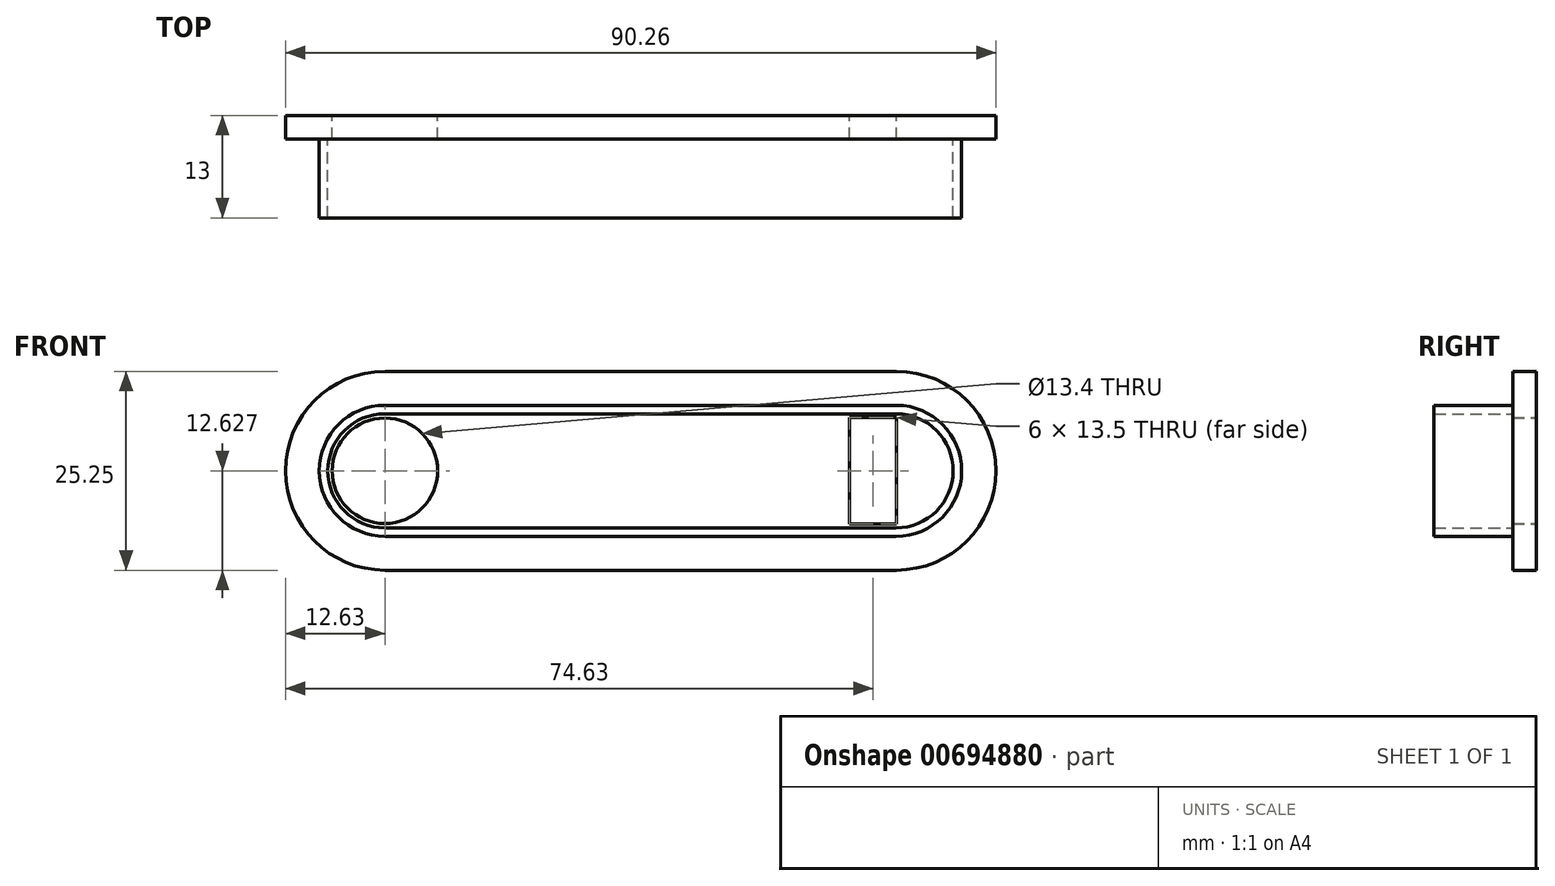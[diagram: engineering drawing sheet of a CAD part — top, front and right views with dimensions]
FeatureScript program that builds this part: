
annotation { "Feature Type Name" : "Feature", "Feature Type Description" : "" }
export const myFeature = defineFeature(function(context is Context, id is Id, definition is map)
    precondition{}
    {
        {
            var Q0;
            Q0=qCreatedBy(makeId("Front.planeOp"),FACE);
            var sketch = newSketch(context, id + "F0", { "sketchPlane" : qUnion([Q0])});
            skLineSegment(sketch, "E0.bottom", {"start": v(19.83, -12.27) * mm, "end": v(-45.17, -12.27) * mm});
            skLineSegment(sketch, "E0.top", {"start": v(19.83, 12.98) * mm, "end": v(-45.17, 12.98) * mm});
            skArc(sketch, "E1", {"start": v(-45.17, 12.98) * mm, "mid": v(-57.8, 0.36) * mm, "end": v(-45.17, -12.27) * mm});
            skArc(sketch, "E2", {"start": v(19.83, -12.27) * mm, "mid": v(32.46, 0.36) * mm, "end": v(19.83, 12.98) * mm});
            skCircle(sketch, "E3", {"center": v(-45.17, 0.36) * mm, "radius": 6.7 * mm});
            skLineSegment(sketch, "E4", {"start": v(19.83, 7.6) * mm, "end": v(12.83, 7.6) * mm});
            skLineSegment(sketch, "E5", {"start": v(12.83, 7.6) * mm, "end": v(19.83, 7.6) * mm});
            skLineSegment(sketch, "E6", {"start": v(19.77, -6.9) * mm, "end": v(12.83, -6.9) * mm});
            skLineSegment(sketch, "E7", {"start": v(19.83, -9.14) * mm, "end": v(19.83, -9.64) * mm});
            skLineSegment(sketch, "E8", {"start": v(13.77, -6.9) * mm, "end": v(19.77, -6.9) * mm});
            skLineSegment(sketch, "E9", {"start": v(19.83, 12.98) * mm, "end": v(19.83, 8.68) * mm});
            skLineSegment(sketch, "E10", {"start": v(19.83, 8.68) * mm, "end": v(-45.17, 8.68) * mm});
            skLineSegment(sketch, "E11", {"start": v(-45.17, -12.27) * mm, "end": v(-45.17, -7.97) * mm});
            skLineSegment(sketch, "E12", {"start": v(-45.17, -7.97) * mm, "end": v(19.77, -7.97) * mm});
            skLineSegment(sketch, "E13", {"start": v(19.77, -6.9) * mm, "end": v(-45.17, -6.9) * mm});
            skLineSegment(sketch, "E14", {"start": v(19.83, 7.6) * mm, "end": v(-45.17, 7.6) * mm});
            skArc(sketch, "E15", {"start": v(-45.17, 8.68) * mm, "mid": v(-53.5, 0.36) * mm, "end": v(-45.17, -7.97) * mm});
            skArc(sketch, "E16", {"start": v(-45.17, 7.6) * mm, "mid": v(-52.42, 0.36) * mm, "end": v(-45.17, -6.9) * mm});
            skLineSegment(sketch, "E17", {"start": v(19.83, 12.98) * mm, "end": v(19.83, -12.27) * mm});
            skPoint(sketch, "E18.middle", {"position": v(16.83, 0.36) * mm});
            skLineSegment(sketch, "E19", {"start": v(19.83, 0.36) * mm, "end": v(19.83, 7.1) * mm});
            skLineSegment(sketch, "E20", {"start": v(19.83, 7.1) * mm, "end": v(13.83, 7.1) * mm});
            skLineSegment(sketch, "E21", {"start": v(13.83, 7.1) * mm, "end": v(13.83, -6.4) * mm});
            skLineSegment(sketch, "E22", {"start": v(13.83, -6.4) * mm, "end": v(19.83, -6.4) * mm});
            skLineSegment(sketch, "E23", {"start": v(19.83, -6.4) * mm, "end": v(19.83, 7.1) * mm});
            skArc(sketch, "E24", {"start": v(19.77, -7.97) * mm, "mid": v(28.1, 0.33) * mm, "end": v(19.83, 8.68) * mm});
            skArc(sketch, "E25", {"start": v(19.77, -6.9) * mm, "mid": v(27.02, 0.33) * mm, "end": v(19.83, 7.6) * mm});
            skSolve(sketch);
        }
        {
            var Q0;
            {var subQ7=sQuery(id+"F0.wireOp",EDGE,"51b1c564-5096-461f-b846-86fedcb4dc8d");Q0=makeQuery(id+"F0.imprint","IMPRINT",FACE,{"disambiguationData":[TD([[makeQuery(id+"F0.imprint","IMPRINT",EDGE,{"derivedFrom":subQ7}),-1.0]])]});}
            var Q1;
            {var subQ2=sQuery(id+"F0.wireOp",EDGE,"E10");Q1=makeQuery(id+"F0.imprint","IMPRINT",FACE,{"disambiguationData":[TD([[makeQuery(id+"F0.imprint","IMPRINT",EDGE,{"derivedFrom":subQ2}),1.0]])]});}
            var Q2;
            {var subQ1=sQuery(id+"F0.wireOp",EDGE,"E17");var subQ3=sQuery(id+"F0.wireOp",EDGE,"E25");var subQ5=makeQuery(id+"F0.imprint","INTERSECT",VERTEX,{"derivedFrom":[subQ1,subQ3]});Q2=makeQuery(id+"F0.imprint","IMPRINT",FACE,{"disambiguationData":[TD([[makeQuery(id+"F0.imprint","IMPRINT",EDGE,{"disambiguationData":[TD([[subQ5,-1.0]])],"derivedFrom":subQ1}),1.0]])]});}
            var Q3;
            Q3=sQuery(id+"F0.wireOp",EDGE,"E0.bottom");
            var Q4;
            Q4=sQuery(id+"F0.wireOp",EDGE,"E0.top");
            var Q5;
            Q5=sQuery(id+"F0.wireOp",EDGE,"E1");
            var Q6;
            Q6=sQuery(id+"F0.wireOp",EDGE,"E2");
            var Q7;
            Q7=sQuery(id+"F0.wireOp",EDGE,"b6ad355e-3722-486a-9c23-38b4642f48d5");
            var Q8;
            Q8=sQuery(id+"F0.wireOp",EDGE,"a5da55c1-d781-4ce2-bdd2-e8d78816f261");
            var Q9;
            Q9=sQuery(id+"F0.wireOp",EDGE,"4fcaac24-b5ef-42e9-b2ac-9cf3cb188516");
            var Q10;
            Q10=sQuery(id+"F0.wireOp",EDGE,"628284f1-229c-46e7-b658-0923db650eb1");
            var Q11;
            Q11=sQuery(id+"F0.wireOp",EDGE,"ba1896cc-4fff-441c-831c-8a4a6f83a2d8");
            var Q12;
            Q12=sQuery(id+"F0.wireOp",EDGE,"E3");
            var Q13;
            Q13=sQuery(id+"F0.wireOp",EDGE,"51b1c564-5096-461f-b846-86fedcb4dc8d");
            var Q14;
            Q14=sQuery(id+"F0.wireOp",EDGE,"6838ca93-eeed-4bdc-afd8-a1c92112be62");
            var Q15;
            Q15=sQuery(id+"F0.wireOp",EDGE,"796d279d-d692-426c-9acc-43a315af8945");
            var Q16;
            Q16=sQuery(id+"F0.wireOp",EDGE,"468f62cb-83c4-4c1b-bd70-739f3564f4d7");
            var Q17;
            Q17=sQuery(id+"F0.wireOp",EDGE,"63cf6457-4c57-4bea-b750-75ee11e2a53f");
            var Q18;
            Q18=sQuery(id+"F0.wireOp",EDGE,"e143a53b-bbf0-4694-9fd8-2c268869048d");
            var Q19;
            Q19=sQuery(id+"F0.wireOp",EDGE,"8f19fd11-0280-4987-803d-bc3ecc1a1e02");
            var Q20;
            Q20=sQuery(id+"F0.wireOp",EDGE,"0b7d8dbc-4690-4e60-8a32-c7cd4177de49");
            var Q21;
            Q21=sQuery(id+"F0.wireOp",EDGE,"E4");
            var Q22;
            Q22=sQuery(id+"F0.wireOp",EDGE,"E5");
            var Q23;
            Q23=sQuery(id+"F0.wireOp",EDGE,"E6");
            var Q24;
            Q24=sQuery(id+"F0.wireOp",EDGE,"3e0e09e5-fe4f-48ed-a0ee-ccac3d4f6891");
            var Q25;
            Q25=sQuery(id+"F0.wireOp",EDGE,"3b197aad-72e7-4fa1-b03a-ef16a77734ec");
            var Q26;
            Q26=sQuery(id+"F0.wireOp",EDGE,"6ab73076-d2da-4c30-87e8-51d7be6df72a.MirrorCS");
            var Q27;
            Q27=sQuery(id+"F0.wireOp",EDGE,"c5502019-c56d-4b6d-b257-b047b59135ca.MirrorCS");
            var Q28;
            Q28=sQuery(id+"F0.wireOp",EDGE,"cbb3f339-5f20-4423-a51a-b7cd7ab5af59.MirrorCS");
            var Q29;
            Q29=sQuery(id+"F0.wireOp",EDGE,"8404de06-89ae-498f-9464-fb25be53e3e3");
            var Q30;
            Q30=sQuery(id+"F0.wireOp",EDGE,"9b76d2de-d04a-4311-8d99-8182bba60f0b");
            var Q31;
            Q31=sQuery(id+"F0.wireOp",EDGE,"E7");
            var Q32;
            Q32=sQuery(id+"F0.wireOp",EDGE,"2683bf00-0369-4066-96d3-9205ea885697.MirrorCS");
            var Q33;
            Q33=sQuery(id+"F0.wireOp",EDGE,"ee40db52-ae8e-40cc-8f7a-23774a43cab0.MirrorCS");
            var Q34;
            Q34=sQuery(id+"F0.wireOp",EDGE,"0a45dc18-5933-418c-8bf1-254a3733ed20");
            var Q35;
            Q35=sQuery(id+"F0.wireOp",EDGE,"7b2331a8-54ae-4d73-9d9e-4a88b023b145");
            var Q36;
            Q36=sQuery(id+"F0.wireOp",EDGE,"46809f8f-a187-47ef-8e81-a9075e9b308d.MirrorCS");
            var Q37;
            Q37=sQuery(id+"F0.wireOp",EDGE,"0649f472-9b76-41c3-96ee-ae1afe34412a");
            var Q38;
            Q38=sQuery(id+"F0.wireOp",EDGE,"a2df31e1-6808-4ee2-9b5d-6a2e88761a76");
            var Q39;
            Q39=sQuery(id+"F0.wireOp",EDGE,"2d52243e-6465-4981-bdd7-aa54638a918c");
            var Q40;
            Q40=sQuery(id+"F0.wireOp",EDGE,"b4da52d1-afe5-4245-a78e-3e48a569191b");
            var Q41;
            Q41=sQuery(id+"F0.wireOp",EDGE,"8c3a6a5f-41b5-48e2-9df0-6684c709de04");
            var Q42;
            Q42=sQuery(id+"F0.wireOp",EDGE,"E8");
            var Q43;
            Q43=sQuery(id+"F0.wireOp",EDGE,"d9717cfd-c6c4-409a-8949-93d3820997f8");
            var Q44;
            Q44=sQuery(id+"F0.wireOp",EDGE,"2369be42-2912-4fa0-8bef-dca674388a07");
            var Q45;
            Q45=sQuery(id+"F0.wireOp",EDGE,"e8eba461-00d1-4ebe-b0c6-392e3b66f3ab");
            var Q46;
            Q46=sQuery(id+"F0.wireOp",EDGE,"d517c2e4-4dd1-45a4-8201-fd70a56d4ab2.MirrorCS");
            var Q47;
            Q47=sQuery(id+"F0.wireOp",EDGE,"d764d433-f32b-435e-9f91-17333f89f89e.MirrorCS");
            var Q48;
            Q48=sQuery(id+"F0.wireOp",EDGE,"f6749d55-f9eb-413d-964b-c2a5628265d1");
            var Q49;
            Q49=sQuery(id+"F0.wireOp",EDGE,"f5be3f5e-2788-4409-a526-137a88d8d8ef");
            var Q50;
            Q50=sQuery(id+"F0.wireOp",EDGE,"0f684251-520a-44b1-957b-e27579d4a1f0");
            var Q51;
            Q51=sQuery(id+"F0.wireOp",EDGE,"c7a5c39c-1b0b-4a4a-88da-ec04e7e83813.MirrorCS");
            var Q52;
            Q52=sQuery(id+"F0.wireOp",EDGE,"7b29877e-e8ec-47ef-aae3-1ecf5dd4d296");
            var Q53;
            Q53=sQuery(id+"F0.wireOp",EDGE,"60b2dc27-ba91-47fd-8fbf-82972dfe182a");
            var Q54;
            Q54=sQuery(id+"F0.wireOp",EDGE,"6d5d4693-0161-4eca-bdc4-8bd8034641af.MirrorCS");
            var Q55;
            Q55=sQuery(id+"F0.wireOp",EDGE,"80347630-f4fb-4bff-a239-73b94e31b8cd");
            var Q56;
            Q56=sQuery(id+"F0.wireOp",EDGE,"1c31f251-1da2-4dbe-a835-6572f029e871");
            var Q57;
            Q57=sQuery(id+"F0.wireOp",EDGE,"d073e572-fe62-4dc8-aaa2-b6fb507d7334");
            var Q58;
            Q58=sQuery(id+"F0.wireOp",EDGE,"72bd91f6-9f3a-4d47-baf1-9d0a996ad9bc.MirrorCS");
            var Q59;
            Q59=sQuery(id+"F0.wireOp",EDGE,"fa604bde-742b-428d-bc45-14590a00dffd.MirrorCS");
            var Q60;
            Q60=sQuery(id+"F0.wireOp",EDGE,"93ab860a-2c70-4860-aebc-eebb65ccb867.MirrorCS");
            extrude(context, id + "F1", {"entities" : qUnion([Q0, Q1, Q2]), "surfaceEntities" : qUnion([Q3, Q4, Q5, Q6, Q7, Q8, Q9, Q10, Q11, Q12, Q13, Q14, Q15, Q16, Q17, Q18, Q19, Q20, Q21, Q22, Q23, Q24, Q25, Q26, Q27, Q28, Q29, Q30, Q31, Q32, Q33, Q34, Q35, Q36, Q37, Q38, Q39, Q40, Q41, Q42, Q43, Q44, Q45, Q46, Q47, Q48, Q49, Q50, Q51, Q52, Q53, Q54, Q55, Q56, Q57, Q58, Q59, Q60]), "depth" : 13 * mm, "offsetDistance" : 25 * mm});
        }
        {
            var Q0;
            {var subQ3=sQuery(id+"F0.wireOp",EDGE,"E2");var subQ4=sQuery(id+"F0.wireOp",EDGE,"E0.bottom");Q0=qUnion([makeQuery(id+"F0.imprint","IMPRINT",FACE,{"disambiguationData":[TD([[makeQuery(id+"F0.imprint","IMPRINT",EDGE,{"derivedFrom":subQ4}),-1.0]])]}),makeQuery(id+"F0.imprint","IMPRINT",FACE,{"disambiguationData":[TD([[makeQuery(id+"F0.imprint","IMPRINT",EDGE,{"derivedFrom":sQuery(id+"F0.wireOp",EDGE,"E0.top")}),1.0]])]}),makeQuery(id+"F0.imprint","IMPRINT",FACE,{"disambiguationData":[TD([[makeQuery(id+"F0.imprint","IMPRINT",EDGE,{"derivedFrom":subQ3}),1.0]])]})]);}
            var Q1;
            Q1=makeQuery(id+"F0.imprint","IMPRINT",FACE,{"disambiguationData":[TD([[makeQuery(id+"F0.imprint","IMPRINT",EDGE,{"derivedFrom":sQuery(id+"F0.wireOp",EDGE,"E3")}),-1.0]])]});
            var Q2;
            {var subQ1=sQuery(id+"F0.wireOp",EDGE,"E17");var subQ6=makeQuery(id+"F0.imprint","IMPRINT",VERTEX,{"derivedFrom":subQ1});Q2=makeQuery(id+"F0.imprint","IMPRINT",FACE,{"disambiguationData":[TD([[makeQuery(id+"F0.imprint","IMPRINT",EDGE,{"disambiguationData":[TD([[subQ6,1.0]])],"derivedFrom":subQ1}),1.0]])]});}
            extrude(context, id + "F2", {"entities" : qUnion([Q0, Q1, Q2]), "operationType" : NewBodyOperationType.ADD, "depth" : 3 * mm, "offsetDistance" : 25 * mm});
        }
    });
